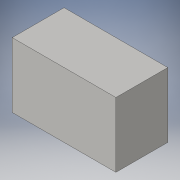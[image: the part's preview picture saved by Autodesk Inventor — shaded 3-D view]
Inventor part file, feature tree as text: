
AUTODESK INVENTOR PART (.ipt)
format: ipt  version: 2016 (Build 200138000, 138)  size: 80,384 bytes
history: native  units: in
note: dims shown in document units (in); Inventor stores cm internally (conversion verified against a paired STEP export)
features: extrude x1, sketch x1
ambient origin geometry x8: Origin, YZ Plane, XZ Plane, XY Plane, X Axis, Y Axis, Z Axis, Center Point
bodies: Solid1 (feature_tree)
feature tree (2):
  extrude  "Extrusion1"  Depth=1.25in
  sketch  "Sketch1"  dims[d0=2.0in d1=1.25in d2=1.0in d3=0.0in]
